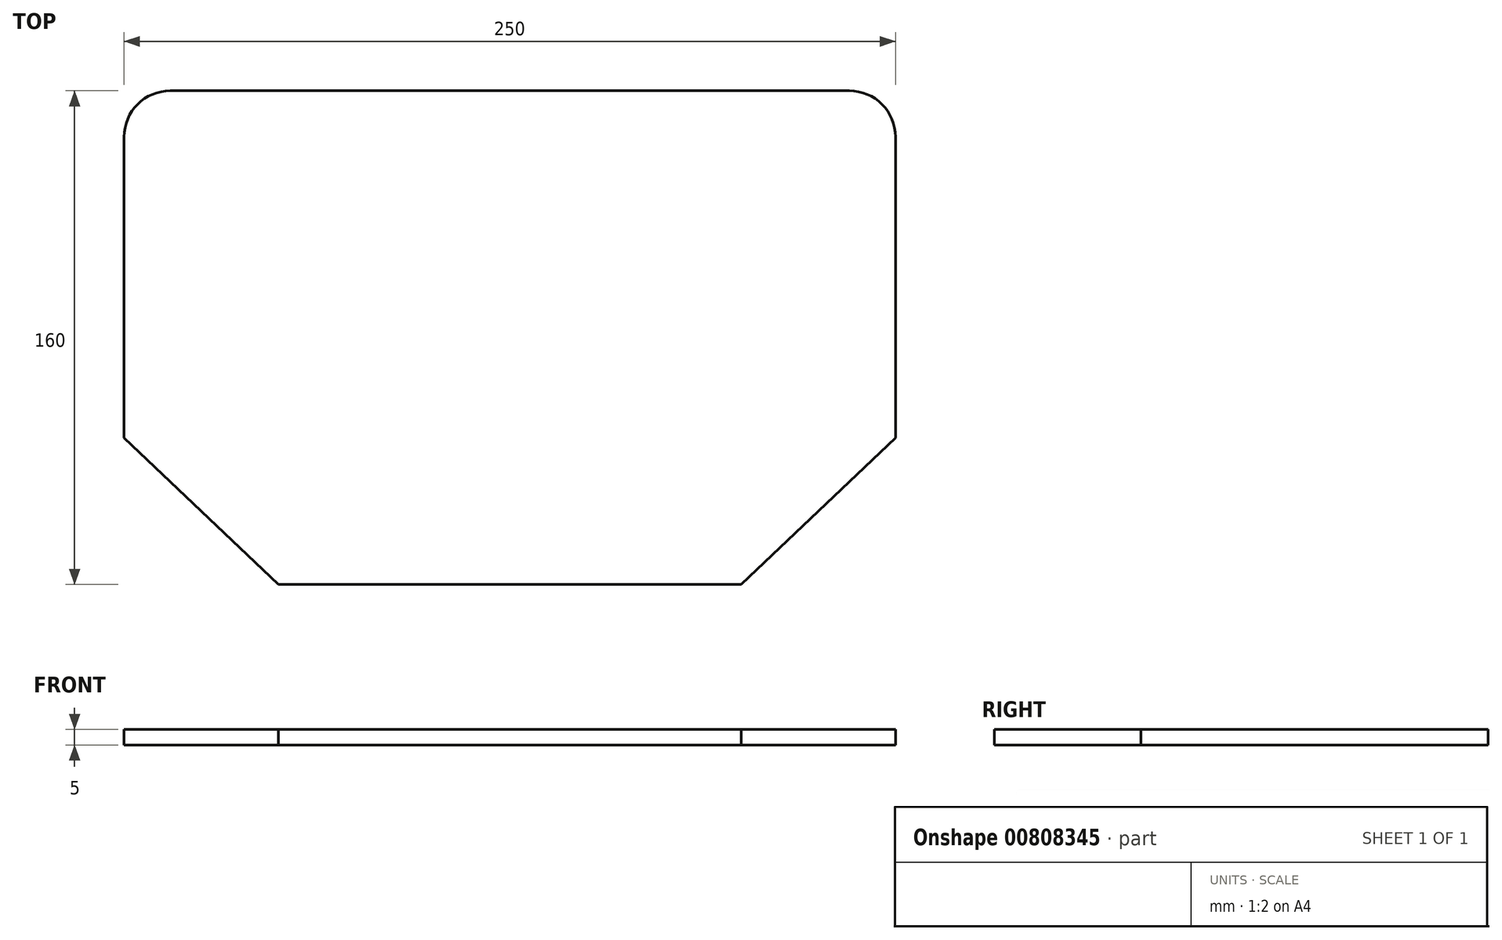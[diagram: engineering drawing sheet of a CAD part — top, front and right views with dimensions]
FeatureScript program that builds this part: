
annotation { "Feature Type Name" : "Feature", "Feature Type Description" : "" }
export const myFeature = defineFeature(function(context is Context, id is Id, definition is map)
    precondition{}
    {
        {
            var Q0;
            Q0=qCreatedBy(makeId("Top.planeOp"),FACE);
            var sketch = newSketch(context, id + "F0", { "sketchPlane" : qUnion([Q0])});
            skLineSegment(sketch, "E0.bottom", {"start": v(50, -1.6) * mm, "end": v(200, -1.6) * mm});
            skLineSegment(sketch, "E0.top", {"start": v(15, 158.4) * mm, "end": v(235, 158.4) * mm});
            skLineSegment(sketch, "E0.left", {"start": v(0, 45.9) * mm, "end": v(0, 143.4) * mm});
            skLineSegment(sketch, "E0.right", {"start": v(250, 45.9) * mm, "end": v(250, 143.4) * mm});
            skLineSegment(sketch, "E1", {"start": v(50, -1.6) * mm, "end": v(0, 45.9) * mm});
            skLineSegment(sketch, "E2", {"start": v(200, -1.6) * mm, "end": v(250, 45.9) * mm});
            skPoint(sketch, "E3.visualSharp", {"position": v(0, 158.4) * mm});
            skArc(sketch, "E3.filletArc", {"start": v(15, 158.4) * mm, "mid": v(4.4, 154) * mm, "end": v(0, 143.4) * mm});
            skPoint(sketch, "E4.visualSharp", {"position": v(250, 158.4) * mm});
            skArc(sketch, "E4.filletArc", {"start": v(250, 143.4) * mm, "mid": v(245.6, 154) * mm, "end": v(235, 158.4) * mm});
            skSolve(sketch);
        }
        {
            var Q0;
            Q0=makeQuery(id+"F0.imprint","IMPRINT",FACE,{"disambiguationData":[TD([[makeQuery(id+"F0.imprint","IMPRINT",EDGE,{"derivedFrom":sQuery(id+"F0.wireOp",EDGE,"E0.bottom")}),1.0]])]});
            extrude(context, id + "F1", {"entities" : qUnion([Q0]), "depth" : 5 * mm, "offsetDistance" : 25 * mm});
        }
    });
